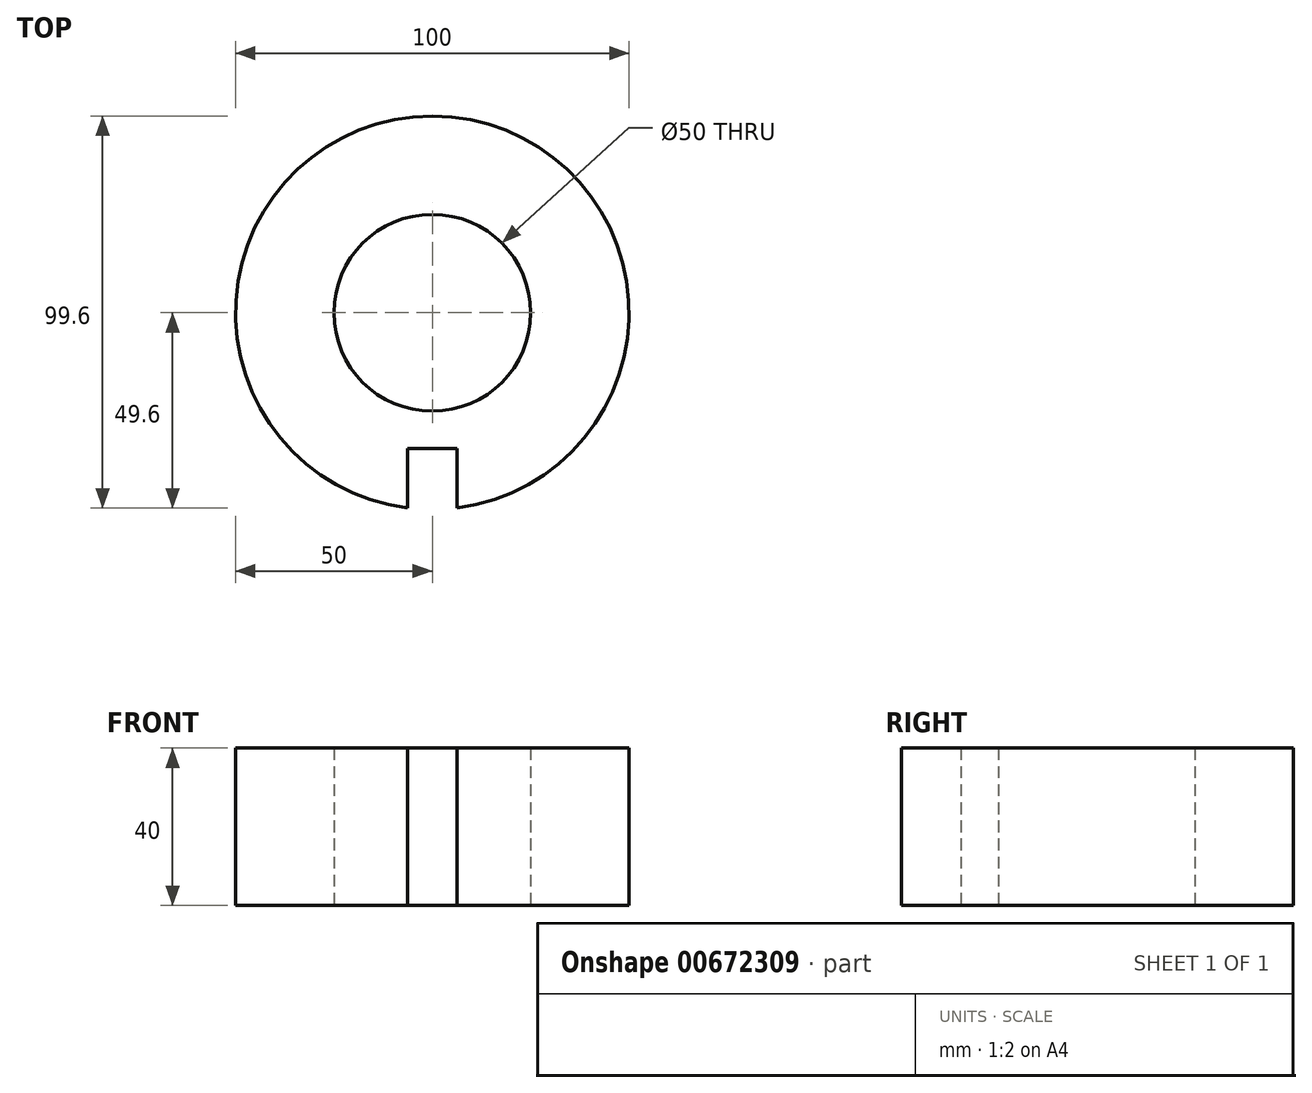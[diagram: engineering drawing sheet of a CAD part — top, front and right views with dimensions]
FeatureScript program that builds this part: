
annotation { "Feature Type Name" : "Feature", "Feature Type Description" : "" }
export const myFeature = defineFeature(function(context is Context, id is Id, definition is map)
    precondition{}
    {
        {
            var Q0;
            Q0=qCreatedBy(makeId("Top.planeOp"),FACE);
            var sketch = newSketch(context, id + "F0", { "sketchPlane" : qUnion([Q0])});
            skArc(sketch, "E0", {"start": v(6.3, -49.6) * mm, "mid": v(0, 50) * mm, "end": v(-6.3, -49.6) * mm});
            skCircle(sketch, "E1", {"center": v(0, 0) * mm, "radius": 25 * mm});
            skLineSegment(sketch, "E2.bottom", {"start": v(6.3, -34.46) * mm, "end": v(-6.3, -34.46) * mm});
            skLineSegment(sketch, "E2.left", {"start": v(6.3, -34.46) * mm, "end": v(6.3, -49.6) * mm});
            skLineSegment(sketch, "E2.right", {"start": v(-6.3, -34.46) * mm, "end": v(-6.3, -49.6) * mm});
            skSolve(sketch);
        }
        {
            var Q0;
            Q0=makeQuery(id+"F0.imprint","IMPRINT",FACE,{"disambiguationData":[TD([[makeQuery(id+"F0.imprint","IMPRINT",EDGE,{"derivedFrom":sQuery(id+"F0.wireOp",EDGE,"E0")}),1.0]])]});
            extrude(context, id + "F1", {"entities" : qUnion([Q0]), "depth" : 40 * mm, "offsetDistance" : 25 * mm});
        }
    });
